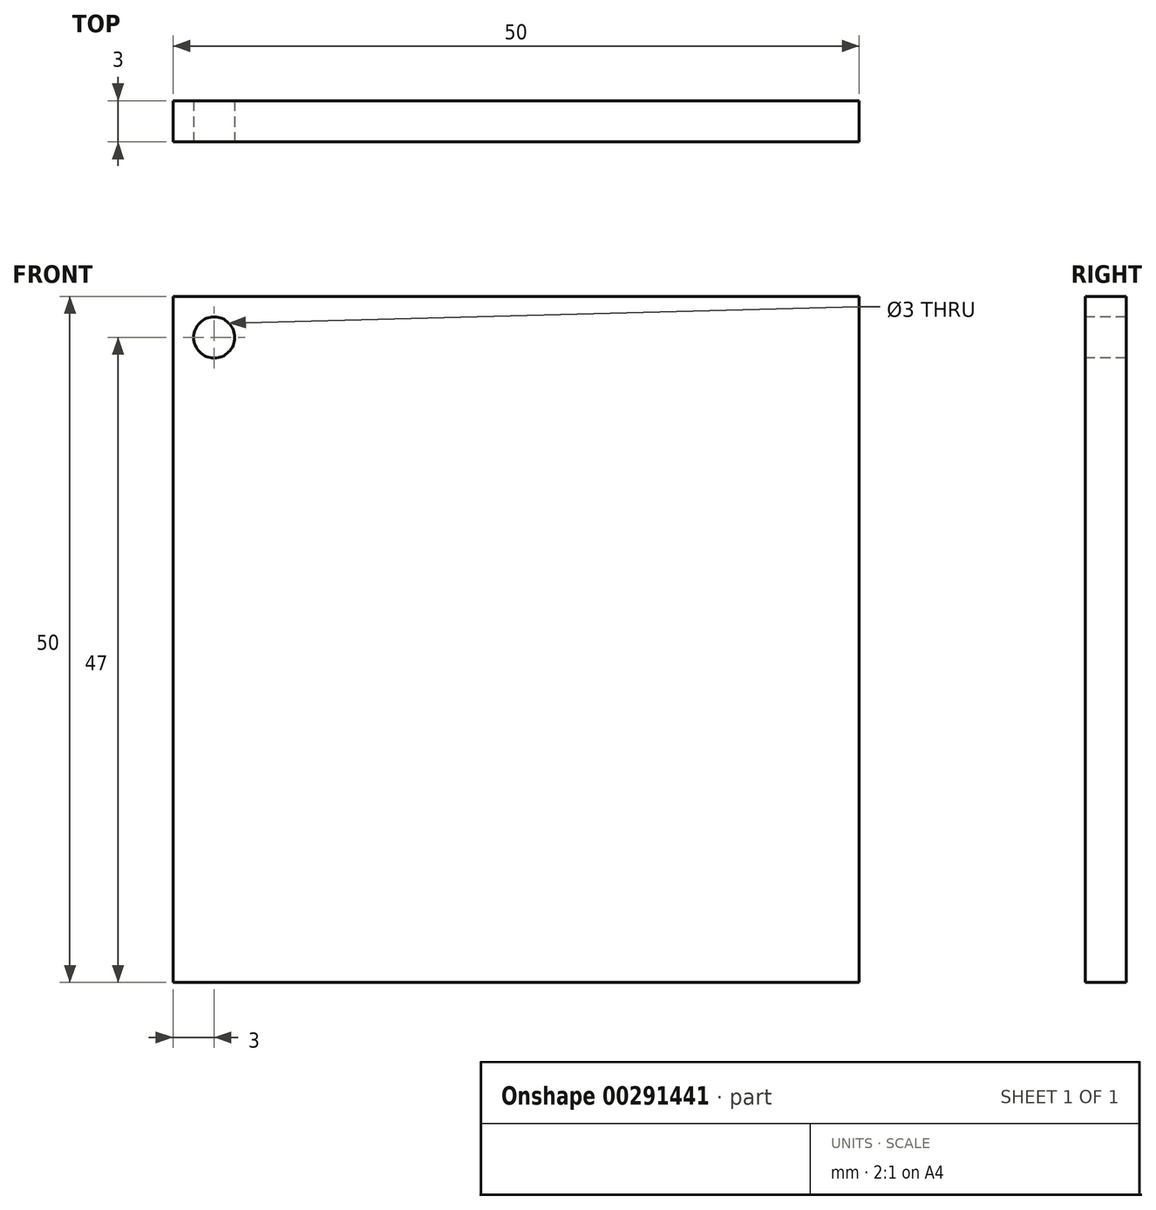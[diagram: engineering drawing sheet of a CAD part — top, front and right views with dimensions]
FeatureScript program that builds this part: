
annotation { "Feature Type Name" : "Feature", "Feature Type Description" : "" }
export const myFeature = defineFeature(function(context is Context, id is Id, definition is map)
    precondition{}
    {
        {
            var Q0;
            Q0=qCreatedBy(makeId("Front.planeOp"),FACE);
            var sketch = newSketch(context, id + "F0", { "sketchPlane" : qUnion([Q0])});
            skLineSegment(sketch, "E0.bottom", {"start": v(25, -25) * mm, "end": v(-25, -25) * mm});
            skLineSegment(sketch, "E0.top", {"start": v(25, 25) * mm, "end": v(-25, 25) * mm});
            skLineSegment(sketch, "E0.left", {"start": v(25, -25) * mm, "end": v(25, 25) * mm});
            skLineSegment(sketch, "E0.right", {"start": v(-25, -25) * mm, "end": v(-25, 25) * mm});
            skPoint(sketch, "E0.middle", {"position": v(0, 0) * mm});
            skSolve(sketch);
        }
        {
            var Q0;
            Q0=makeQuery(id+"F0.imprint","IMPRINT",FACE,{"disambiguationData":[TD([[makeQuery(id+"F0.imprint","IMPRINT",EDGE,{"derivedFrom":sQuery(id+"F0.wireOp",EDGE,"E0.bottom")}),-1.0]])]});
            extrude(context, id + "F1", {"entities" : qUnion([Q0]), "depth" : 3 * mm});
        }
        {
            var Q0;
            Q0=makeQuery(id+"F1.opExtrude","CAP_FACE",FACE,{"disambiguationData":[OSD([sQuery(id+"F0.wireOp",EDGE,"E0.bottom"),sQuery(id+"F0.wireOp",EDGE,"E0.top"),sQuery(id+"F0.wireOp",EDGE,"E0.left"),sQuery(id+"F0.wireOp",EDGE,"E0.right")])],"isStart":false});
            var sketch = newSketch(context, id + "F2", { "sketchPlane" : qUnion([Q0])});
            skCircle(sketch, "E1", {"center": v(-22, 22) * mm, "radius": 1.5 * mm});
            skSolve(sketch);
        }
        {
            var Q0;
            Q0 = qSketchRegion(id + "F2", true);
            extrude(context, id + "F3", {"entities" : qUnion([Q0]), "operationType" : NewBodyOperationType.REMOVE, "oppositeDirection" : true, "depth" : 25 * mm});
        }
    });
